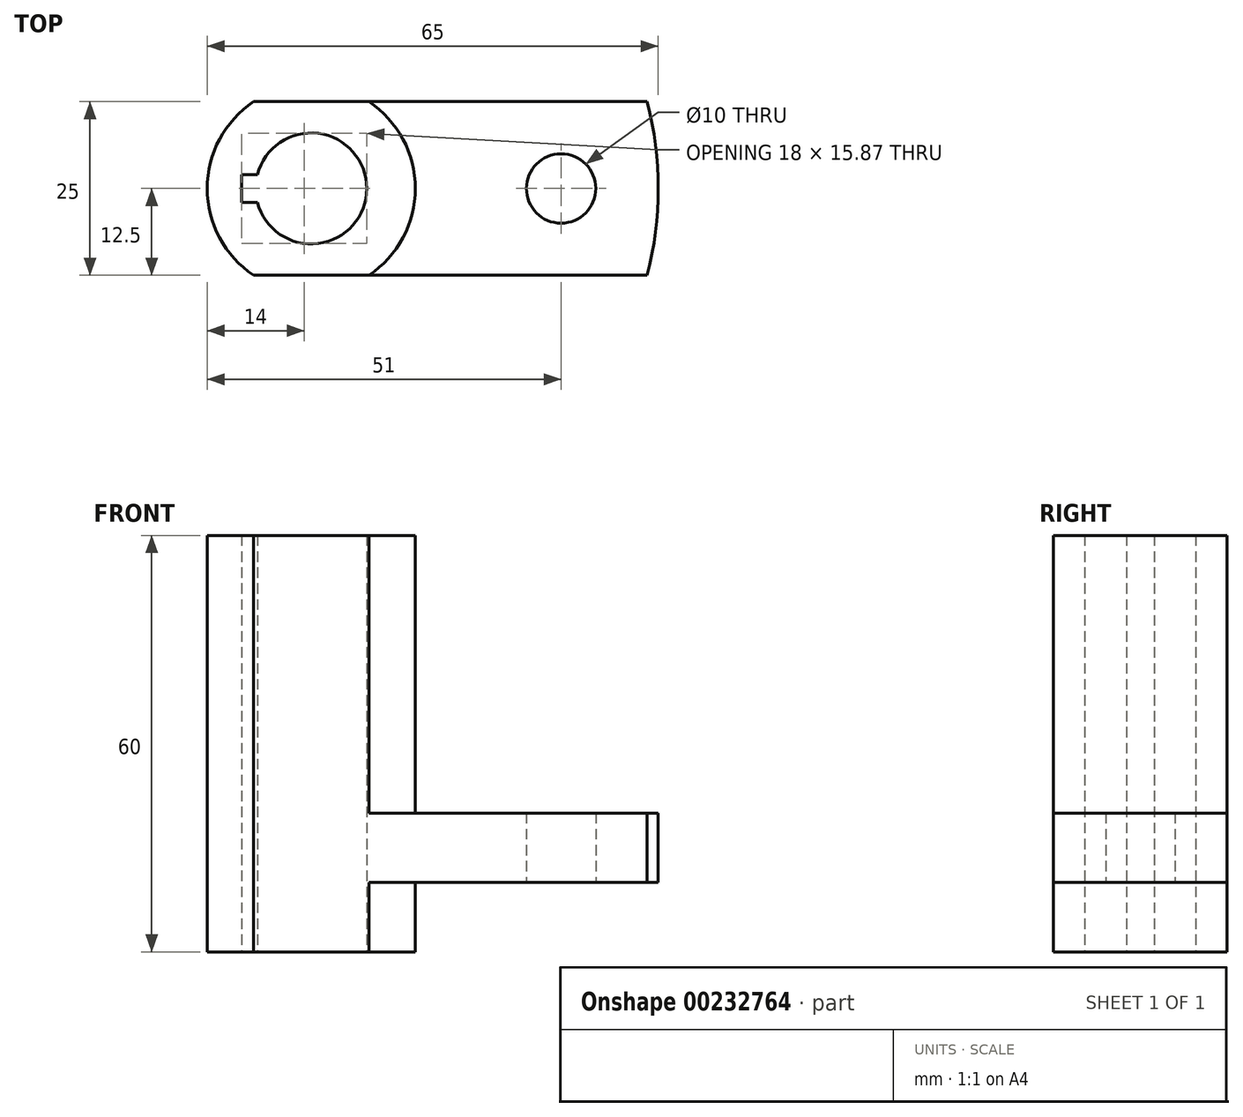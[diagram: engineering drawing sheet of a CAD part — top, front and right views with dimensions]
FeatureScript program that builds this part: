
annotation { "Feature Type Name" : "Feature", "Feature Type Description" : "" }
export const myFeature = defineFeature(function(context is Context, id is Id, definition is map)
    precondition{}
    {
        {
            var Q0;
            Q0=qCreatedBy(makeId("Top.planeOp"),FACE);
            var sketch = newSketch(context, id + "F0", { "sketchPlane" : qUnion([Q0])});
            skLineSegment(sketch, "E0", {"start": v(-75.6, 0) * mm, "end": v(65.45, 0) * mm, "construction": true});
            skLineSegment(sketch, "E1", {"start": v(0, 56.92) * mm, "end": v(0, -43.3) * mm, "construction": true});
            skLineSegment(sketch, "E2.bottom", {"start": v(0, 12.5) * mm, "end": v(48.41, 12.5) * mm});
            skLineSegment(sketch, "E2.top", {"start": v(0, -12.5) * mm, "end": v(48.41, -12.5) * mm});
            skLineSegment(sketch, "E2.right", {"start": v(48.41, 12.5) * mm, "end": v(48.41, -12.5) * mm, "construction": true});
            skArc(sketch, "E3", {"start": v(48.41, -12.5) * mm, "mid": v(50, 0) * mm, "end": v(48.41, 12.5) * mm});
            skArc(sketch, "E4", {"start": v(8.3, -12.5) * mm, "mid": v(15, 0) * mm, "end": v(8.3, 12.5) * mm});
            skCircle(sketch, "E5", {"center": v(36, 0) * mm, "radius": 5 * mm});
            skLineSegment(sketch, "E6.MirrorCS", {"start": v(-48.41, 12.5) * mm, "end": v(-48.41, -12.5) * mm, "construction": true});
            skLineSegment(sketch, "E7.MirrorCS", {"start": v(75.6, 0) * mm, "end": v(-65.45, 0) * mm, "construction": true});
            skLineSegment(sketch, "E8.MirrorCS", {"start": v(0, 12.5) * mm, "end": v(-48.41, 12.5) * mm});
            skLineSegment(sketch, "E9.MirrorCS", {"start": v(0, -12.5) * mm, "end": v(-48.41, -12.5) * mm});
            skArc(sketch, "E10.MirrorCS", {"start": v(-48.41, -12.5) * mm, "mid": v(-50, 0) * mm, "end": v(-48.41, 12.5) * mm});
            skArc(sketch, "E11.MirrorCS", {"start": v(-8.3, -12.5) * mm, "mid": v(-15, 0) * mm, "end": v(-8.3, 12.5) * mm});
            skCircle(sketch, "E12.MirrorC", {"center": v(-36, 0) * mm, "radius": 5 * mm});
            skArc(sketch, "E13", {"start": v(-7.75, -2) * mm, "mid": v(8, 0) * mm, "end": v(-7.75, 2) * mm});
            skLineSegment(sketch, "E14.bottom", {"start": v(-10, 2) * mm, "end": v(-7.75, 2) * mm});
            skLineSegment(sketch, "E14.top", {"start": v(-10, -2) * mm, "end": v(-7.75, -2) * mm});
            skLineSegment(sketch, "E14.left", {"start": v(-10, 2) * mm, "end": v(-10, -2) * mm});
            skSolve(sketch);
        }
        {
            var Q0;
            {var subQ4=sQuery(id+"F0.wireOp",EDGE,"E4");Q0=makeQuery(id+"F0.imprint","IMPRINT",FACE,{"disambiguationData":[TD([[makeQuery(id+"F0.imprint","IMPRINT",EDGE,{"derivedFrom":subQ4}),1.0]])]});}
            extrude(context, id + "F1", {"entities" : qUnion([Q0]), "depth" : 50 * mm});
        }
        {
            var Q0;
            {var subQ4=sQuery(id+"F0.wireOp",EDGE,"E4");Q0=makeQuery(id+"F0.imprint","IMPRINT",FACE,{"disambiguationData":[TD([[makeQuery(id+"F0.imprint","IMPRINT",EDGE,{"derivedFrom":subQ4}),1.0]])]});}
            extrude(context, id + "F2", {"entities" : qUnion([Q0]), "operationType" : NewBodyOperationType.ADD, "oppositeDirection" : true, "depth" : 10 * mm});
        }
        {
            var Q0;
            {var subQ1=sQuery(id+"F0.wireOp",EDGE,"E10.MirrorCS");Q0=makeQuery(id+"F0.imprint","IMPRINT",FACE,{"disambiguationData":[TD([[makeQuery(id+"F0.imprint","IMPRINT",EDGE,{"derivedFrom":subQ1}),-1.0]])]});}
            var Q1;
            {var subQ1=sQuery(id+"F0.wireOp",EDGE,"E3");Q1=makeQuery(id+"F0.imprint","IMPRINT",FACE,{"disambiguationData":[TD([[makeQuery(id+"F0.imprint","IMPRINT",EDGE,{"derivedFrom":subQ1}),1.0]])]});}
            extrude(context, id + "F3", {"entities" : qUnion([Q0, Q1]), "operationType" : NewBodyOperationType.ADD, "depth" : 10 * mm});
        }
    });
